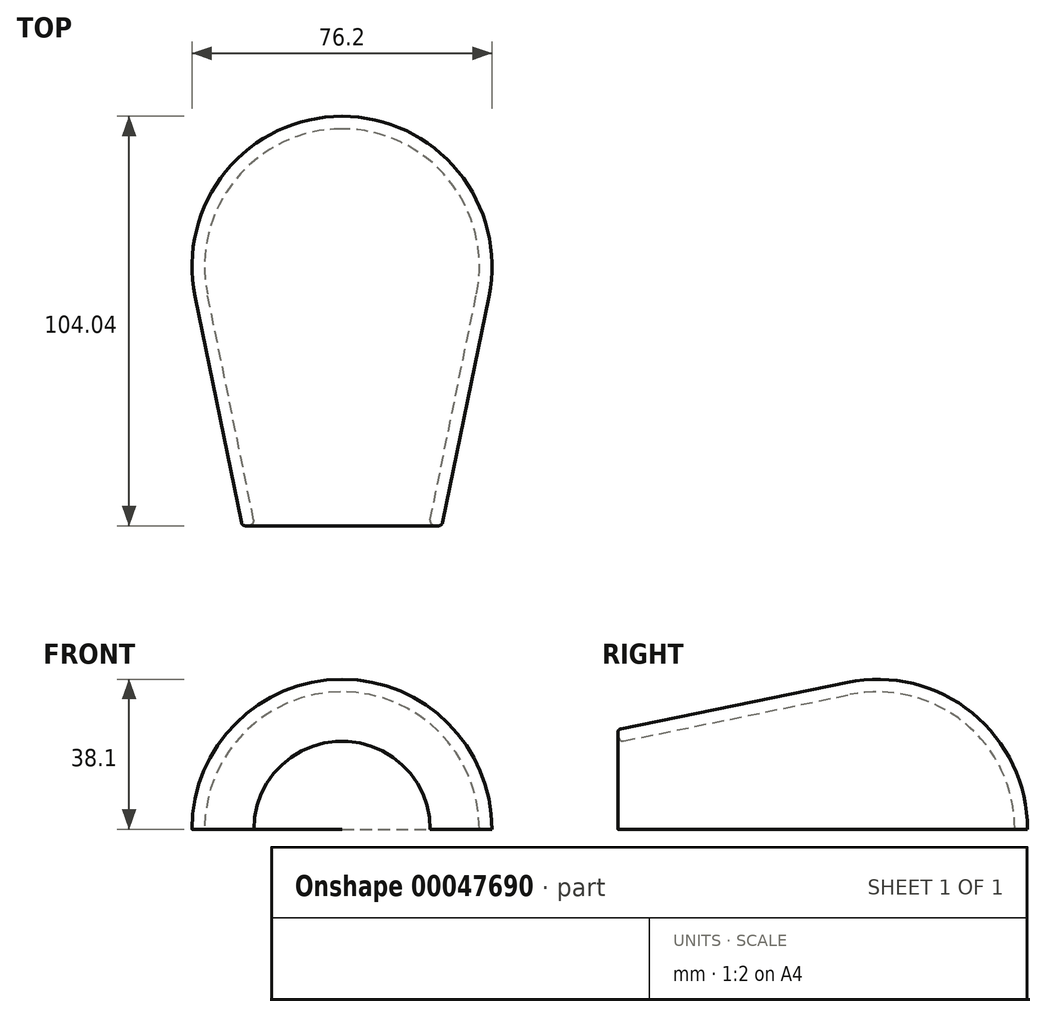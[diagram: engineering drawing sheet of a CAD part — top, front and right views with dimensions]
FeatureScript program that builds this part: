
annotation { "Feature Type Name" : "Feature", "Feature Type Description" : "" }
export const myFeature = defineFeature(function(context is Context, id is Id, definition is map)
    precondition{}
    {
        {
            var Q0;
            Q0=qCreatedBy(makeId("Top.planeOp"),FACE);
            var sketch = newSketch(context, id + "F0", { "sketchPlane" : qUnion([Q0])});
            skArc(sketch, "E0", {"start": v(0, 38.1) * mm, "mid": v(-29.52, 24.09) * mm, "end": v(-37.33, -7.65) * mm});
            skLineSegment(sketch, "E1", {"start": v(-25.4, -65.86) * mm, "end": v(-37.33, -7.65) * mm});
            skLineSegment(sketch, "E2", {"start": v(0, 38.1) * mm, "end": v(0, 34.9) * mm});
            skArc(sketch, "E3.0", {"start": v(0, 34.9) * mm, "mid": v(-27.04, 22.06) * mm, "end": v(-34.2, -7) * mm});
            skLineSegment(sketch, "E3.1", {"start": v(-22.27, -65.22) * mm, "end": v(-34.2, -7) * mm});
            skArc(sketch, "E4", {"start": v(-25.4, -65.86) * mm, "mid": v(-23.77, -65.86) * mm, "end": v(-22.27, -65.22) * mm});
            skPoint(sketch, "E4.third.point", {"position": v(-23.2, -65.7) * mm});
            skSolve(sketch);
        }
        {
            var Q0;
            Q0=makeQuery(id+"F0.imprint","IMPRINT",FACE,{"disambiguationData":[TD([[makeQuery(id+"F0.imprint","IMPRINT",EDGE,{"derivedFrom":sQuery(id+"F0.wireOp",EDGE,"E0")}),1.0]])]});
            var Q1;
            Q1=sQuery(id+"F0.wireOp",EDGE,"E2");
            revolve(context, id + "F1", {"entities" : qUnion([Q0]), "axis" : qUnion([Q1]), "revolveType" : RevolveType.ONE_DIRECTION, "oppositeDirection" : true, "angle" : 180 * degree});
        }
        {
            var Q0;
            Q0=makeQuery(id+"F1.opRevolve","SWEPT_EDGE",EDGE,{"disambiguationData":[OSD([sQuery(id+"F0.wireOp",EDGE,"E3.1"),sQuery(id+"F0.wireOp",EDGE,"E4")])]});
            var Q1;
            Q1=makeQuery(id+"F1.opRevolve","SWEPT_EDGE",EDGE,{"disambiguationData":[OSD([sQuery(id+"F0.wireOp",EDGE,"E1"),sQuery(id+"F0.wireOp",EDGE,"E4")])]});
            fillet(context, id + "F2", {"entities" : qUnion([Q0, Q1]), "radius" : 1 * mm, "tangentPropagation" : true, "allowEdgeOverflow" : false});
        }
    });
